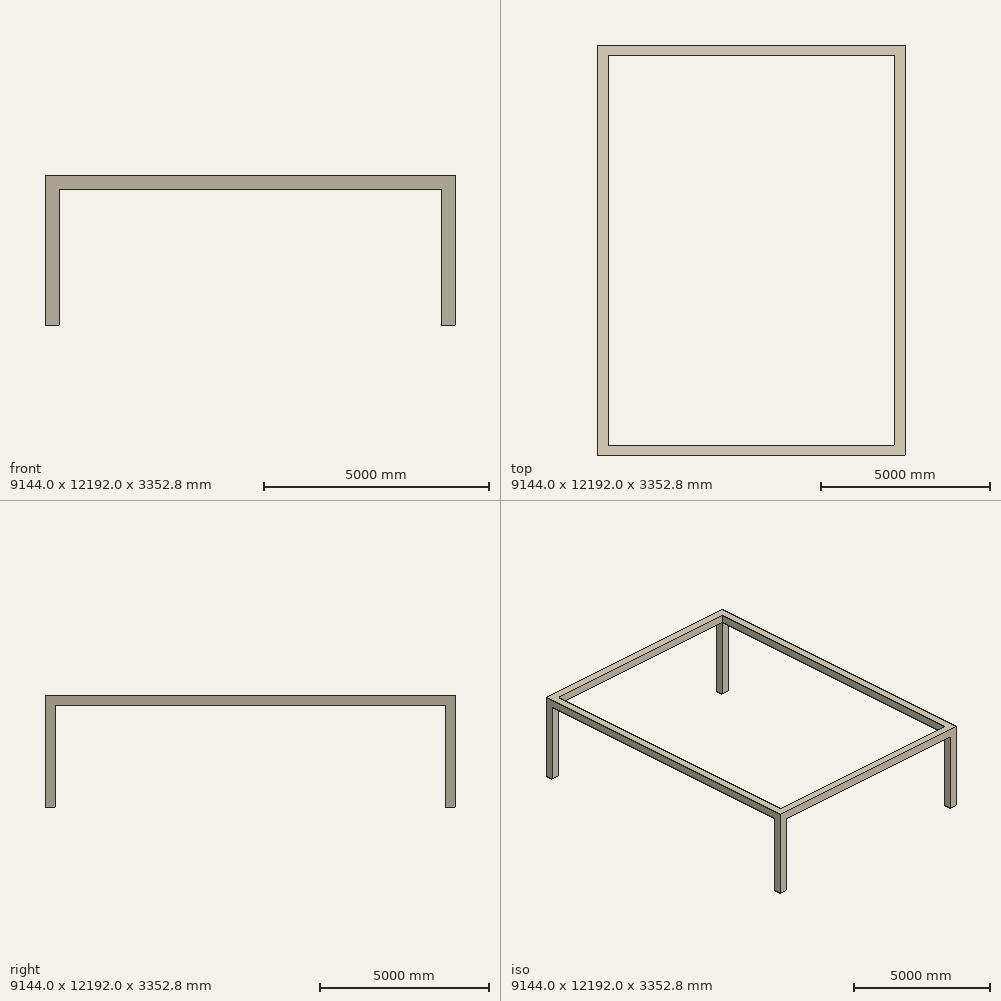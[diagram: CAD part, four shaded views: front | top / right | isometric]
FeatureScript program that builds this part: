
annotation { "Feature Type Name" : "Feature", "Feature Type Description" : "" }
export const myFeature = defineFeature(function(context is Context, id is Id, definition is map)
    precondition{}
    {
        {
            var Q0;
            Q0=qCreatedBy(makeId("Top.planeOp"),FACE);
            var sketch = newSketch(context, id + "F0", { "sketchPlane" : qUnion([Q0])});
            skLineSegment(sketch, "E0.bottom", {"start": v(4572, -6096) * mm, "end": v(-4572, -6096) * mm});
            skLineSegment(sketch, "E0.top", {"start": v(4572, 6096) * mm, "end": v(-4572, 6096) * mm});
            skLineSegment(sketch, "E0.left", {"start": v(4572, -6096) * mm, "end": v(4572, 6096) * mm});
            skLineSegment(sketch, "E0.right", {"start": v(-4572, -6096) * mm, "end": v(-4572, 6096) * mm});
            skPoint(sketch, "E0.middle", {"position": v(0, 0) * mm});
            skLineSegment(sketch, "E1.bottom", {"start": v(4267.2, -5791.2) * mm, "end": v(-4267.2, -5791.2) * mm});
            skLineSegment(sketch, "E1.top", {"start": v(4267.2, 5791.2) * mm, "end": v(-4267.2, 5791.2) * mm});
            skLineSegment(sketch, "E1.left", {"start": v(4267.2, -5791.2) * mm, "end": v(4267.2, 5791.2) * mm});
            skLineSegment(sketch, "E1.right", {"start": v(-4267.2, -5791.2) * mm, "end": v(-4267.2, 5791.2) * mm});
            skSolve(sketch);
        }
        {
            var Q0;
            Q0=makeQuery(id+"F0.imprint","IMPRINT",FACE,{"disambiguationData":[TD([[makeQuery(id+"F0.imprint","IMPRINT",EDGE,{"derivedFrom":sQuery(id+"F0.wireOp",EDGE,"E0.bottom")}),-1.0]])]});
            extrude(context, id + "F1", {"entities" : qUnion([Q0]), "depth" : 304.8 * mm, "offsetDistance" : 30.48 * mm});
        }
        {
            var Q0;
            Q0=makeQuery(id+"F1.opExtrude","CAP_FACE",FACE,{"disambiguationData":[OSD([sQuery(id+"F0.wireOp",EDGE,"E0.bottom"),sQuery(id+"F0.wireOp",EDGE,"E0.top"),sQuery(id+"F0.wireOp",EDGE,"E0.left"),sQuery(id+"F0.wireOp",EDGE,"E0.right"),sQuery(id+"F0.wireOp",EDGE,"E1.bottom"),sQuery(id+"F0.wireOp",EDGE,"E1.top"),sQuery(id+"F0.wireOp",EDGE,"E1.left"),sQuery(id+"F0.wireOp",EDGE,"E1.right")])],"isStart":true});
            var sketch = newSketch(context, id + "F2", { "sketchPlane" : qUnion([Q0])});
            skLineSegment(sketch, "E2", {"start": v(0, 6180.74) * mm, "end": v(0, -4569.7) * mm, "construction": true});
            skLineSegment(sketch, "E3", {"start": v(-3348.31, 0) * mm, "end": v(2621.26, 0) * mm, "construction": true});
            skPoint(sketch, "E3.endSnap0", {"position": v(4267.2, 0) * mm});
            skLineSegment(sketch, "E4.bottom", {"start": v(-4572, 6096) * mm, "end": v(-4267.2, 6096) * mm});
            skLineSegment(sketch, "E4.top", {"start": v(-4572, 5791.2) * mm, "end": v(-4267.2, 5791.2) * mm});
            skLineSegment(sketch, "E4.left", {"start": v(-4572, 6096) * mm, "end": v(-4572, 5791.2) * mm});
            skLineSegment(sketch, "E4.right", {"start": v(-4267.2, 6096) * mm, "end": v(-4267.2, 5791.2) * mm});
            skLineSegment(sketch, "E5.MirrorCS", {"start": v(4572, 6096) * mm, "end": v(4267.2, 6096) * mm});
            skLineSegment(sketch, "E6.MirrorCS", {"start": v(4572, 5791.2) * mm, "end": v(4267.2, 5791.2) * mm});
            skLineSegment(sketch, "E7.MirrorCS", {"start": v(4572, 6096) * mm, "end": v(4572, 5791.2) * mm});
            skLineSegment(sketch, "E8.MirrorCS", {"start": v(4267.2, 6096) * mm, "end": v(4267.2, 5791.2) * mm});
            skLineSegment(sketch, "E9.MirrorCS", {"start": v(4572, -6096) * mm, "end": v(4267.2, -6096) * mm});
            skLineSegment(sketch, "E10.MirrorCS", {"start": v(-4267.2, -6096) * mm, "end": v(-4267.2, -5791.2) * mm});
            skLineSegment(sketch, "E11.MirrorCS", {"start": v(-4572, -6096) * mm, "end": v(-4572, -5791.2) * mm});
            skLineSegment(sketch, "E12.MirrorCS", {"start": v(-4572, -5791.2) * mm, "end": v(-4267.2, -5791.2) * mm});
            skLineSegment(sketch, "E13.MirrorCS", {"start": v(-4572, -6096) * mm, "end": v(-4267.2, -6096) * mm});
            skLineSegment(sketch, "E14.MirrorCS", {"start": v(4267.2, -6096) * mm, "end": v(4267.2, -5791.2) * mm});
            skLineSegment(sketch, "E15.MirrorCS", {"start": v(4572, -6096) * mm, "end": v(4572, -5791.2) * mm});
            skLineSegment(sketch, "E16.MirrorCS", {"start": v(4572, -5791.2) * mm, "end": v(4267.2, -5791.2) * mm});
            skSolve(sketch);
        }
        {
            var Q0;
            Q0 = qSketchRegion(id + "F2", true);
            extrude(context, id + "F3", {"entities" : qUnion([Q0]), "operationType" : NewBodyOperationType.ADD, "depth" : 3048 * mm, "offsetDistance" : 30.48 * mm});
        }
    });
